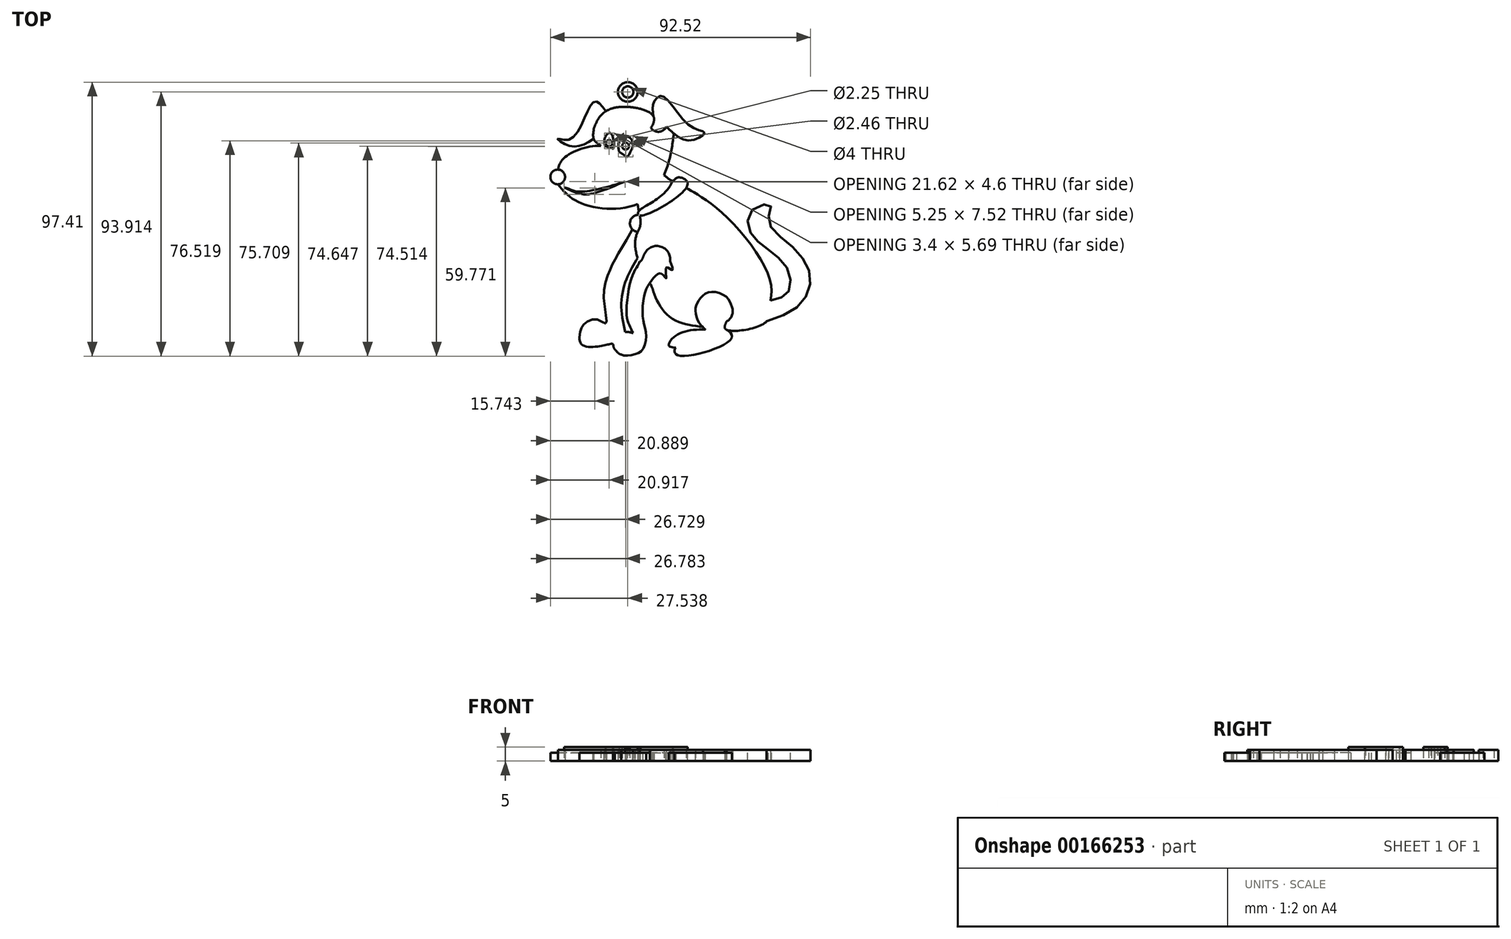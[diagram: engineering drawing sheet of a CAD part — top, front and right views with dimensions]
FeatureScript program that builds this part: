
annotation { "Feature Type Name" : "Feature", "Feature Type Description" : "" }
export const myFeature = defineFeature(function(context is Context, id is Id, definition is map)
    precondition{}
    {
        {
            var Q0;
            Q0=qCreatedBy(makeId("Top.planeOp"),FACE);
            var sketch = newSketch(context, id + "F0", { "sketchPlane" : qUnion([Q0])});
            skFitSpline(sketch, "E0", {"points": [v(-44.31, 22.49) * mm, v(-41.94, 26.77) * mm, v(-29.07, 30.97) * mm, v(-19.57, 26.94) * mm], "startDerivative": vector(5, 18.2) * mm, "endDerivative": vector(25.56, -15.85) * mm});
            skFitSpline(sketch, "E1", {"points": [v(-29.07, 30.97) * mm, v(-31.59, 33.44) * mm, v(-29.07, 41.7) * mm, v(-19.39, 44.77) * mm, v(-10.34, 41.43) * mm, v(-11.2, 37.33) * mm], "startDerivative": vector(-19.93, 16.9) * mm, "endDerivative": vector(-14.54, -23.38) * mm});
            skFitSpline(sketch, "E2", {"points": [v(-10.34, 41.43) * mm, v(-10.34, 46) * mm, v(-7.29, 48.62) * mm, v(2.73, 37.93) * mm, v(7.75, 35.56) * mm, v(2.47, 32.85) * mm, v(-5.78, 37.72) * mm], "startDerivative": vector(-5.78, 33.55) * mm, "endDerivative": vector(-40.96, 36.4) * mm});
            skFitSpline(sketch, "E3", {"points": [v(-27.23, 43.25) * mm, v(-31.59, 46.51) * mm, v(-39.65, 33.44) * mm, v(-44.44, 33.44) * mm, v(-40.38, 30.97) * mm, v(-31.59, 33.44) * mm], "startDerivative": vector(-26.1, 36.1) * mm, "endDerivative": vector(40.33, 27.84) * mm});
            skFitSpline(sketch, "E4", {"points": [v(-3.11, 35.35) * mm, v(-5.78, 22.49) * mm, v(-16, 10.27) * mm, v(-36.48, 10.7) * mm, v(-44.31, 17.26) * mm], "startDerivative": vector(-6.26, -53.57) * mm, "endDerivative": vector(-29.01, 35.12) * mm});
            skFitSpline(sketch, "E5", {"points": [v(-43.92, 17.06) * mm, v(-38.7, 14.62) * mm, v(-33.73, 13.66) * mm, v(-20.44, 18.25) * mm], "startDerivative": vector(19.6, -9.43) * mm, "endDerivative": vector(33.68, 14.1) * mm});
            skCircle(sketch, "E6", {"center": v(-44.37, 19.87) * mm, "radius": 2.61 * mm});
            skPoint(sketch, "E6.third.point", {"position": v(-46.99, 19.76) * mm});
            skFitSpline(sketch, "E7", {"points": [v(-22.57, 28.8) * mm, v(-22.57, 32.64) * mm, v(-20.26, 34.53) * mm, v(-17.65, 32.13) * mm, v(-19.57, 26.94) * mm], "startDerivative": vector(-2.87, 19.17) * mm, "endDerivative": vector(-11.72, -20.66) * mm});
            skFitSpline(sketch, "E8", {"points": [v(-27.55, 30.8) * mm, v(-27.67, 33.44) * mm, v(-26, 35.56) * mm, v(-24.62, 33.44) * mm, v(-24.6, 29.85) * mm], "startDerivative": vector(-1.9, 13.5) * mm, "endDerivative": vector(-3.26, -15.34) * mm});
            skCircle(sketch, "E9", {"center": v(-20.26, 30.83) * mm, "radius": 1.23 * mm});
            skCircle(sketch, "E10", {"center": v(-26.1, 31.89) * mm, "radius": 1.13 * mm});
            skFitSpline(sketch, "E11", {"points": [v(-6.55, 20.57) * mm, v(-3.37, 18.55) * mm, v(-1.83, 19.64) * mm, v(1.8, 17.28) * mm, v(-15.13, 6.14) * mm, v(-15.56, 7.65) * mm, v(-3.58, 18.33) * mm], "startDerivative": vector(29.11, -25.7) * mm, "endDerivative": vector(32.2, 74.32) * mm});
            skFitSpline(sketch, "E12", {"points": [v(1.27, 15.96) * mm, v(4.64, 14.04) * mm, v(16.93, 4.43) * mm, v(31.32, -17.45) * mm, v(30.5, -27.1) * mm], "startDerivative": vector(20.47, -11.46) * mm, "endDerivative": vector(-10.6, -41.95) * mm});
            skFitSpline(sketch, "E13", {"points": [v(30.58, -26.9) * mm, v(29.9, -31.4) * mm, v(15.48, -34.36) * mm, v(15.63, -31.55) * mm], "startDerivative": vector(-5.59, -10.55) * mm, "endDerivative": vector(6.52, 15.6) * mm});
            skFitSpline(sketch, "E14", {"points": [v(15.48, -34.36) * mm, v(17.21, -37.8) * mm, v(-1.96, -43.46) * mm, v(-2.4, -40.85) * mm, v(0, -39.98) * mm], "startDerivative": vector(23.52, -11.55) * mm, "endDerivative": vector(16.48, 1.54) * mm});
            skFitSpline(sketch, "E15", {"points": [v(-2.4, -40.85) * mm, v(-4.8, -40.06) * mm, v(-2.4, -36.54) * mm, v(8.14, -34.36) * mm], "startDerivative": vector(-13.87, 1.08) * mm, "endDerivative": vector(24.07, -0.6) * mm});
            skFitSpline(sketch, "E16", {"points": [v(8.14, -34.36) * mm, v(5.67, -31.55) * mm, v(4.6, -27.1) * mm, v(5.83, -24.02) * mm, v(9.52, -21.1) * mm, v(15.63, -22.8) * mm, v(17.53, -26.33) * mm], "startDerivative": vector(-17.43, 16.62) * mm, "endDerivative": vector(6.98, -23.6) * mm});
            skFitSpline(sketch, "E17", {"points": [v(-15.13, 6.14) * mm, v(-15.13, 2.16) * mm, v(-16.84, -2.87) * mm, v(-15.13, -10.1) * mm, v(-13.6, -7.68) * mm], "startDerivative": vector(1.95, -17.51) * mm, "endDerivative": vector(7.74, 18.83) * mm});
            skFitSpline(sketch, "E18", {"points": [v(-11.6, -17.85) * mm, v(-9.41, -23.34) * mm, v(-3.09, -30.84) * mm, v(7.24, -33.51) * mm], "startDerivative": vector(7.77, -9.43) * mm, "endDerivative": vector(27.4, -4.17) * mm});
            skFitSpline(sketch, "E19", {"points": [v(-15.13, -10.1) * mm, v(-15.94, -11.74) * mm, v(-17.86, -15.19) * mm, v(-19.85, -29.46) * mm, v(-18.76, -33.07) * mm, v(-17.64, -35.66) * mm], "startDerivative": vector(-9.3, -14.04) * mm, "endDerivative": vector(6.78, -15.79) * mm});
            skFitSpline(sketch, "E20", {"points": [v(-17.64, -35.66) * mm, v(-23.45, -35.66) * mm, v(-24.68, -37.72) * mm, v(-24.06, -41.42) * mm, v(-21.75, -40.8) * mm], "startDerivative": vector(-13.32, 5.48) * mm, "endDerivative": vector(14.76, 8.37) * mm});
            skFitSpline(sketch, "E21", {"points": [v(-24.06, -41.42) * mm, v(-21.75, -43.27) * mm, v(-18.76, -41.42) * mm], "startDerivative": vector(4.62, -5.67) * mm, "endDerivative": vector(6.44, 5.46) * mm});
            skFitSpline(sketch, "E22", {"points": [v(-21.75, -43.27) * mm, v(-17.83, -43.37) * mm, v(-14.1, -41.38) * mm, v(-12.99, -35.66) * mm, v(-14.1, -30.16) * mm, v(-13.47, -21.79) * mm, v(-11.6, -17.85) * mm, v(-7.6, -14.46) * mm, v(-5.78, -16.17) * mm, v(-5.78, -12.32) * mm, v(-3.75, -13.23) * mm, v(-4.37, -10.1) * mm], "startDerivative": vector(24.62, -21.12) * mm, "endDerivative": vector(-24.11, 63.1) * mm});
            skFitSpline(sketch, "E23", {"points": [v(-16, 10.27) * mm, v(-15.56, 7.65) * mm], "startDerivative": vector(0.44, -2.61) * mm, "endDerivative": vector(0.44, -2.61) * mm});
            skArc(sketch, "E24", {"start": v(-4.37, -10.1) * mm, "mid": v(-7.93, -4.83) * mm, "end": v(-13.6, -7.68) * mm});
            skArc(sketch, "E25", {"start": v(-11.2, 37.33) * mm, "mid": v(-8.37, 35.92) * mm, "end": v(-5.78, 37.72) * mm});
            skArc(sketch, "E26", {"start": v(15.63, -31.55) * mm, "mid": v(17.62, -29.32) * mm, "end": v(17.53, -26.33) * mm});
            skLineSegment(sketch, "E27", {"start": v(-3.58, 18.33) * mm, "end": v(-3.37, 18.55) * mm});
            skArc(sketch, "E28", {"start": v(-15.73, 6.4) * mm, "mid": v(-18.7, 3.44) * mm, "end": v(-15.91, 0.3) * mm});
            skFitSpline(sketch, "E29", {"points": [v(-17.84, 1.22) * mm, v(-22.48, -6.84) * mm, v(-25.9, -13.42) * mm, v(-27.98, -23.36) * mm, v(-27.25, -32.16) * mm, v(-30.18, -30.87) * mm, v(-34.76, -32.16) * mm, v(-36.41, -35.27) * mm, v(-35.86, -39.67) * mm, v(-30, -40.4) * mm, v(-26.34, -39.67) * mm, v(-24.68, -39.53) * mm], "startDerivative": vector(-12.56, -30.57) * mm, "endDerivative": vector(30.3, -9.9) * mm});
            skFitSpline(sketch, "E30", {"points": [v(-15.94, -8.92) * mm, v(-19.37, -15.19) * mm, v(-21.76, -24.83) * mm, v(-20.36, -35.2) * mm], "startDerivative": vector(-11.66, -19.55) * mm, "endDerivative": vector(6.43, -28.01) * mm});
            skFitSpline(sketch, "E31", {"points": [v(31.27, -24.02) * mm, v(37.39, -21.37) * mm, v(37.67, -13.6) * mm, v(30.5, -5.92) * mm, v(24.2, 0) * mm, v(24.5, 7.85) * mm, v(31.27, 9.86) * mm, v(30.5, 4.45) * mm, v(37.59, -3.73) * mm, v(45.17, -13.87) * mm, v(43.05, -24.02) * mm, v(29.9, -31.4) * mm], "startDerivative": vector(101.66, 21.62) * mm, "endDerivative": vector(-149.41, -43.02) * mm});
            skFitSpline(sketch, "E32", {"points": [v(-42.06, 16.16) * mm, v(-38.25, 14.82) * mm, v(-33.73, 14.82) * mm, v(-27.47, 16.15) * mm, v(-20.44, 18.25) * mm], "startDerivative": vector(17.76, -4.5) * mm, "endDerivative": vector(24.55, 7.68) * mm});
            skFitSpline(sketch, "E33", {"points": [v(-36.64, -37.14) * mm, v(-33.9, -34.06) * mm, v(-30, -35.27) * mm], "startDerivative": vector(4.86, 8.3) * mm, "endDerivative": vector(8.42, -4.57) * mm});
            skLineSegment(sketch, "E34", {"start": v(-17.84, 1.22) * mm, "end": v(-17.84, 1.22) * mm});
            skArc(sketch, "E35", {"start": v(-16.9, 44.49) * mm, "mid": v(-19.45, 48.82) * mm, "end": v(-22.4, 44.74) * mm});
            skCircle(sketch, "E36", {"center": v(-19.45, 50.1) * mm, "radius": 3.5 * mm});
            skPoint(sketch, "E36.centerSnap0", {"position": v(-19.45, 48.82) * mm});
            skCircle(sketch, "E37.0", {"center": v(-19.45, 50.1) * mm, "radius": 2 * mm});
            skSolve(sketch);
        }
        {
            var Q0;
            {var subQ16=sQuery(id+"F0.wireOp",EDGE,"E7");Q0=makeQuery(id+"F0.imprint","IMPRINT",FACE,{"disambiguationData":[TD([[makeQuery(id+"F0.imprint","IMPRINT",EDGE,{"derivedFrom":subQ16}),1.0]])]});}
            var Q1;
            {var subQ0=sQuery(id+"F0.wireOp",EDGE,"E23");Q1=makeQuery(id+"F0.imprint","IMPRINT",FACE,{"disambiguationData":[TD([[makeQuery(id+"F0.imprint","IMPRINT",EDGE,{"derivedFrom":subQ0}),1.0]])]});}
            var Q2;
            {var subQ9=sQuery(id+"F0.wireOp",EDGE,"E18");Q2=makeQuery(id+"F0.imprint","IMPRINT",FACE,{"disambiguationData":[TD([[makeQuery(id+"F0.imprint","IMPRINT",EDGE,{"derivedFrom":subQ9}),1.0]])]});}
            var Q3;
            {var subQ0=sQuery(id+"F0.wireOp",EDGE,"E19");Q3=makeQuery(id+"F0.imprint","IMPRINT",FACE,{"disambiguationData":[TD([[makeQuery(id+"F0.imprint","IMPRINT",EDGE,{"derivedFrom":subQ0}),-1.0]])]});}
            var Q4;
            {var subQ3=sQuery(id+"F0.wireOp",EDGE,"E31");Q4=makeQuery(id+"F0.imprint","IMPRINT",FACE,{"disambiguationData":[TD([[makeQuery(id+"F0.imprint","IMPRINT",EDGE,{"derivedFrom":subQ3}),-1.0]])]});}
            var Q5;
            {var subQ0=sQuery(id+"F0.wireOp",EDGE,"E36");var subQ1=sQuery(id+"F0.wireOp",EDGE,"E35");var subQ2=makeQuery(id+"F0.imprint","INTERSECT",VERTEX,{"disambiguationData":[OD(0.0)],"derivedFrom":[subQ1,subQ0]});Q5=makeQuery(id+"F0.imprint","IMPRINT",FACE,{"disambiguationData":[TD([[makeQuery(id+"F0.imprint","IMPRINT",EDGE,{"disambiguationData":[TD([[subQ2,-1.0]])],"derivedFrom":subQ1}),-1.0]])]});}
            var Q6;
            {var subQ0=sQuery(id+"F0.wireOp",EDGE,"E35");var subQ1=sQuery(id+"F0.wireOp",EDGE,"E1");var subQ2=makeQuery(id+"F0.imprint","INTERSECT",VERTEX,{"disambiguationData":[OD(0.0)],"derivedFrom":[subQ1,subQ0]});Q6=makeQuery(id+"F0.imprint","IMPRINT",FACE,{"disambiguationData":[TD([[makeQuery(id+"F0.imprint","IMPRINT",EDGE,{"disambiguationData":[TD([[subQ2,1.0]])],"derivedFrom":subQ1}),1.0]])]});}
            var Q7;
            {var subQ0=sQuery(id+"F0.wireOp",EDGE,"E36");var subQ1=sQuery(id+"F0.wireOp",EDGE,"E35");var subQ2=makeQuery(id+"F0.imprint","INTERSECT",VERTEX,{"disambiguationData":[OD(0.0)],"derivedFrom":[subQ1,subQ0]});Q7=makeQuery(id+"F0.imprint","IMPRINT",FACE,{"disambiguationData":[TD([[makeQuery(id+"F0.imprint","IMPRINT",EDGE,{"disambiguationData":[TD([[subQ2,-1.0]])],"derivedFrom":subQ1}),1.0]])]});}
            extrude(context, id + "F1", {"entities" : qUnion([Q0, Q1, Q2, Q3, Q4, Q5, Q6, Q7]), "depth" : 4 * mm});
        }
        {
            var Q0;
            {var subQ0=sQuery(id+"F0.wireOp",EDGE,"E3");Q0=makeQuery(id+"F0.imprint","IMPRINT",FACE,{"disambiguationData":[TD([[makeQuery(id+"F0.imprint","IMPRINT",EDGE,{"derivedFrom":subQ0}),1.0]])]});}
            var Q1;
            {var subQ0=sQuery(id+"F0.wireOp",EDGE,"E25");Q1=makeQuery(id+"F0.imprint","IMPRINT",FACE,{"disambiguationData":[TD([[makeQuery(id+"F0.imprint","IMPRINT",EDGE,{"derivedFrom":subQ0}),1.0]])]});}
            var Q2;
            {var subQ4=sQuery(id+"F0.wireOp",EDGE,"E19");Q2=makeQuery(id+"F0.imprint","IMPRINT",FACE,{"disambiguationData":[TD([[makeQuery(id+"F0.imprint","IMPRINT",EDGE,{"derivedFrom":subQ4}),1.0]])]});}
            var Q3;
            {var subQ8=sQuery(id+"F0.wireOp",EDGE,"E30");Q3=makeQuery(id+"F0.imprint","IMPRINT",FACE,{"disambiguationData":[TD([[makeQuery(id+"F0.imprint","IMPRINT",EDGE,{"derivedFrom":subQ8}),-1.0]])]});}
            var Q4;
            {var subQ0=sQuery(id+"F0.wireOp",EDGE,"E15");Q4=makeQuery(id+"F0.imprint","IMPRINT",FACE,{"disambiguationData":[TD([[makeQuery(id+"F0.imprint","IMPRINT",EDGE,{"derivedFrom":subQ0}),-1.0]])]});}
            var Q5;
            {var subQ0=sQuery(id+"F0.wireOp",EDGE,"E6");var subQ1=makeQuery(id+"F0.imprint","INTERSECT",VERTEX,{"derivedFrom":[sQuery(id+"F0.wireOp",EDGE,"E0"),subQ0]});Q5=makeQuery(id+"F0.imprint","IMPRINT",FACE,{"disambiguationData":[TD([[makeQuery(id+"F0.imprint","IMPRINT",EDGE,{"disambiguationData":[TD([[subQ1,-1.0]])],"derivedFrom":subQ0}),1.0]])]});}
            extrude(context, id + "F2", {"entities" : qUnion([Q0, Q1, Q2, Q3, Q4, Q5]), "depth" : 3 * mm});
        }
        {
            var Q0;
            Q0=makeQuery(id+"F0.imprint","IMPRINT",FACE,{"disambiguationData":[TD([[makeQuery(id+"F0.imprint","IMPRINT",EDGE,{"derivedFrom":sQuery(id+"F0.wireOp",EDGE,"E5")}),1.0]])]});
            var Q1;
            {var subQ0=sQuery(id+"F0.wireOp",EDGE,"E7");Q1=makeQuery(id+"F0.imprint","IMPRINT",FACE,{"disambiguationData":[TD([[makeQuery(id+"F0.imprint","IMPRINT",EDGE,{"derivedFrom":subQ0}),-1.0]])]});}
            var Q2;
            {var subQ0=sQuery(id+"F0.wireOp",EDGE,"E8");Q2=makeQuery(id+"F0.imprint","IMPRINT",FACE,{"disambiguationData":[TD([[makeQuery(id+"F0.imprint","IMPRINT",EDGE,{"derivedFrom":subQ0}),-1.0]])]});}
            var Q3;
            {var subQ5=sQuery(id+"F0.wireOp",EDGE,"E27");Q3=makeQuery(id+"F0.imprint","IMPRINT",FACE,{"disambiguationData":[TD([[makeQuery(id+"F0.imprint","IMPRINT",EDGE,{"derivedFrom":subQ5}),-1.0]])]});}
            var Q4;
            {var subQ0=sQuery(id+"F0.wireOp",EDGE,"E17");var subQ1=sQuery(id+"F0.wireOp",EDGE,"E11");var subQ2=makeQuery(id+"F0.imprint","INTERSECT",VERTEX,{"derivedFrom":[subQ1,subQ0]});Q4=makeQuery(id+"F0.imprint","IMPRINT",FACE,{"disambiguationData":[TD([[makeQuery(id+"F0.imprint","IMPRINT",EDGE,{"disambiguationData":[TD([[subQ2,-1.0]])],"derivedFrom":subQ1}),1.0]])]});}
            extrude(context, id + "F3", {"entities" : qUnion([Q0, Q1, Q2, Q3, Q4]), "depth" : 5 * mm});
        }
    });
